# Revit family: Shower-Bath_and_Shower_Trim-KOHLER-July-K-TS98006_1
name_source: partatom
category: Plumbing Fixtures
revit_build: Autodesk Revit 2017 (Build: 20160225_1515(x64)
units: mm (PartAtom-declared; Revit-internal decimal feet)

## family parameters
Cut with Voids When Loaded = No
Host = Face
OmniClass Number = 23.31.17.00
Part Type = Normal
Room Calculation Point = No
Round Connector Dimension = Use Diameter
Shared = No

## types (4) — shared parameters
ADA Compliant = No
Assembly Code = D2010700
CW Connection = No
Cold Water Inlet = Cold Water Inlet
Date Modified = 01/02/2020
Default Elevation = 42"
Drain Included = No
Flow Rate = 2 GPM
HW Connection = Yes
Height = 6 1/2"
Hot Water Inlet = Hot Water Inlet
Length = 7 1/2"
Manufacturer = KOHLER Co.
MasterFormat 1995 = 15410
MasterFormat 2004 = 22.41.23
Material = Premium Metal Construction
Pressure = 80.00 psi
Product Documentation Link = https://www.us.kohler.com
Product Name = July
Product Page URL = http://www.us.kohler.com
Tempered Water Inlet 1 = Tempered Water Inlet 1
Tempered Water Inlet 2 = Tempered Water Inlet 2
URL = https://www.us.kohler.com
Vent Connection = No
Waste Connection = No
Waste Water Outlet = Waste Water Outlet
WaterSense Certified = Yes
Width = 6 1/2"

## per-type parameters (varying)
| type | Description | Finish | Model | Type |
| 2 GPM,CP-Polished Chrome | Rite-Temp bath and shower valve trim with lever handle, slip-fit spout and 2.0 gpm showerhead | Kohler-Metal-CP-Polished_Chrome | K-TS98006-4-CP | 1 |
| 2 GPM,G-Brushed Chrome | Rite-Temp bath and shower valve trim with lever handle, slip-fit spout and 2.0 gpm showerhead | Kohler-Metal-G-Brushed_Chrome | K-TS98006-4-G | 2 |
| 1.75 GPM,CP-Polished Chrome | Rite-Temp bath and shower trim with lever handle, slip-fit spout and 1.75 gpm showerhead | Kohler-Metal-CP-Polished_Chrome | K-TS98006-4G-CP | 3 |
| 1.75 GPM,G-Brushed Chrome | Rite-Temp bath and shower trim with lever handle, slip-fit spout and 1.75 gpm showerhead | Kohler-Metal-G-Brushed_Chrome | K-TS98006-4G-G | 4 |

## geometry (parser evidence)
native form markers: Sweep x11
no freeform markers — native parametric forms only
